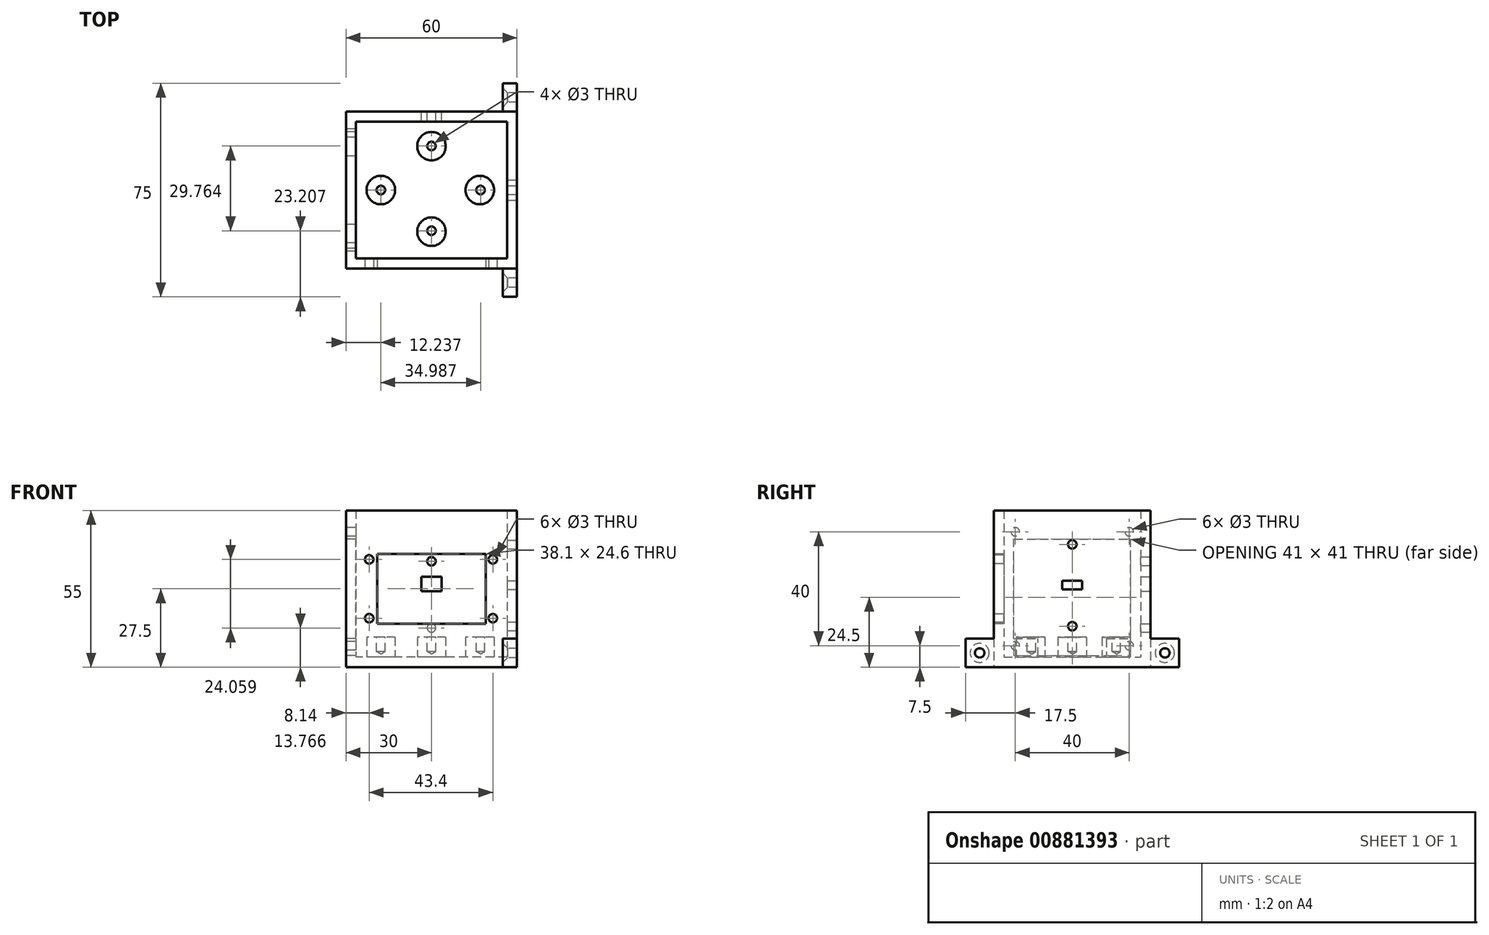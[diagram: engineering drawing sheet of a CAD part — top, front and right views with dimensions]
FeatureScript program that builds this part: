
annotation { "Feature Type Name" : "Feature", "Feature Type Description" : "" }
export const myFeature = defineFeature(function(context is Context, id is Id, definition is map)
    precondition{}
    {
        {
            var Q0;
            Q0=qCreatedBy(makeId("Top.planeOp"),FACE);
            var sketch = newSketch(context, id + "F0", { "sketchPlane" : qUnion([Q0])});
            skLineSegment(sketch, "E0.bottom", {"start": v(30, -27.5) * mm, "end": v(-30, -27.5) * mm});
            skLineSegment(sketch, "E0.top", {"start": v(30, 27.5) * mm, "end": v(-30, 27.5) * mm});
            skLineSegment(sketch, "E0.left", {"start": v(30, -27.5) * mm, "end": v(30, 27.5) * mm});
            skLineSegment(sketch, "E0.right", {"start": v(-30, -27.5) * mm, "end": v(-30, 27.5) * mm});
            skPoint(sketch, "E0.middle", {"position": v(0, 0) * mm});
            skSolve(sketch);
        }
        {
            var Q0;
            Q0=makeQuery(id+"F0.imprint","IMPRINT",FACE,{"disambiguationData":[TD([[makeQuery(id+"F0.imprint","IMPRINT",EDGE,{"derivedFrom":sQuery(id+"F0.wireOp",EDGE,"E0.bottom")}),-1.0]])]});
            extrude(context, id + "F1", {"entities" : qUnion([Q0]), "depth" : 55 * mm, "offsetDistance" : 25 * mm});
        }
        {
            var Q0;
            Q0=makeQuery(id+"F1.opExtrude","CAP_FACE",FACE,{"disambiguationData":[OSD([sQuery(id+"F0.wireOp",EDGE,"E0.bottom"),sQuery(id+"F0.wireOp",EDGE,"E0.top"),sQuery(id+"F0.wireOp",EDGE,"E0.left"),sQuery(id+"F0.wireOp",EDGE,"E0.right")])],"isStart":false});
            shell(context, id + "F2", {"entities" : qUnion([Q0]), "thickness" : 3.5 * mm});
        }
        {
            var Q0;
            Q0=makeQuery(id+"F1.opExtrude","SWEPT_FACE",FACE,{"disambiguationData":[OSD([sQuery(id+"F0.wireOp",EDGE,"E0.bottom")])]});
            var sketch = newSketch(context, id + "F3", { "sketchPlane" : qUnion([Q0])});
            skPoint(sketch, "E1", {"position": v(0, 27.5) * mm});
            skPoint(sketch, "E2", {"position": v(0, 39.8) * mm});
            skPoint(sketch, "E3", {"position": v(0, 15.2) * mm});
            skPoint(sketch, "E4", {"position": v(-19.05, 39.8) * mm});
            skPoint(sketch, "E5", {"position": v(19.05, 39.8) * mm});
            skPoint(sketch, "E6", {"position": v(-19.05, 15.2) * mm});
            skPoint(sketch, "E7", {"position": v(19.05, 15.2) * mm});
            skLineSegment(sketch, "E8", {"start": v(-19.05, 39.8) * mm, "end": v(-19.05, 15.2) * mm});
            skLineSegment(sketch, "E9", {"start": v(0, 15.2) * mm, "end": v(-19.05, 15.2) * mm});
            skLineSegment(sketch, "E10", {"start": v(0, 15.2) * mm, "end": v(19.05, 15.2) * mm});
            skLineSegment(sketch, "E11", {"start": v(19.05, 15.2) * mm, "end": v(19.05, 39.8) * mm});
            skLineSegment(sketch, "E12", {"start": v(-19.05, 39.8) * mm, "end": v(19.05, 39.8) * mm});
            skSolve(sketch);
        }
        {
            var Q0;
            Q0=makeQuery(id+"F3.imprint","IMPRINT",FACE,{"disambiguationData":[TD([[makeQuery(id+"F3.imprint","IMPRINT",EDGE,{"derivedFrom":sQuery(id+"F3.wireOp",EDGE,"E8")}),1.0]])]});
            extrude(context, id + "F4", {"entities" : qUnion([Q0]), "operationType" : NewBodyOperationType.REMOVE, "oppositeDirection" : true, "depth" : 5 * mm, "offsetDistance" : 25 * mm});
        }
        {
            var Q0;
            Q0=makeQuery(id+"F1.opExtrude","SWEPT_FACE",FACE,{"disambiguationData":[OSD([sQuery(id+"F0.wireOp",EDGE,"E0.bottom")])]});
            var sketch = newSketch(context, id + "F5", { "sketchPlane" : qUnion([Q0])});
            skPoint(sketch, "E13", {"position": v(21.54, 37.82) * mm});
            skPoint(sketch, "E14", {"position": v(21.54, 17.17) * mm});
            skPoint(sketch, "E15", {"position": v(-21.86, 17.17) * mm});
            skPoint(sketch, "E16", {"position": v(-21.86, 37.82) * mm});
            skPoint(sketch, "E17", {"position": v(19.05, 27.5) * mm});
            skPoint(sketch, "E18", {"position": v(21.54, 27.5) * mm});
            skSolve(sketch);
        }
        {
            var Q0;
            Q0=sQuery(id+"F5.wireOp",VERTEX,"E16");
            var Q1;
            Q1=sQuery(id+"F5.wireOp",VERTEX,"E15");
            var Q2;
            Q2=sQuery(id+"F5.wireOp",VERTEX,"E14");
            var Q3;
            Q3=sQuery(id+"F5.wireOp",VERTEX,"E13");
            var Q4;
            Q4=makeQuery(id+"F1.opExtrude","SWEPT_BODY",BODY,{"disambiguationData":[OSD([sQuery(id+"F0.wireOp",EDGE,"E0.bottom"),sQuery(id+"F0.wireOp",EDGE,"E0.top"),sQuery(id+"F0.wireOp",EDGE,"E0.left"),sQuery(id+"F0.wireOp",EDGE,"E0.right")])]});
            hole(context, id + "F6", {"style" : HoleStyle.SIMPLE, "endStyle" : HoleEndStyle.BLIND, "holeDiameter" : 3 * mm, "majorDiameter" : 5 * mm, "holeDepth" : 12 * mm, "isTappedThrough" : true, "tappedDepth" : 12 * mm, "tapClearance" : 3, "startFromSketch" : true, "locations" : qUnion([Q0, Q1, Q2, Q3]), "scope" : qUnion([Q4])});
        }
        {
            var Q0;
            Q0=makeQuery(id+"F1.opExtrude","SWEPT_FACE",FACE,{"disambiguationData":[OSD([sQuery(id+"F0.wireOp",EDGE,"E0.right")])]});
            var sketch = newSketch(context, id + "F7", { "sketchPlane" : qUnion([Q0])});
            skPoint(sketch, "E19", {"position": v(0, 27.5) * mm});
            skLineSegment(sketch, "E20.bottom", {"start": v(20.5, 10) * mm, "end": v(-20.5, 10) * mm});
            skLineSegment(sketch, "E20.top", {"start": v(20.5, 45) * mm, "end": v(-20.5, 45) * mm});
            skLineSegment(sketch, "E20.left", {"start": v(20.5, 10) * mm, "end": v(20.5, 45) * mm});
            skLineSegment(sketch, "E20.right", {"start": v(-20.5, 10) * mm, "end": v(-20.5, 45) * mm});
            skPoint(sketch, "E21", {"position": v(20, 27.5) * mm});
            skPoint(sketch, "E22", {"position": v(20, 47.5) * mm});
            skPoint(sketch, "E23", {"position": v(20, 7.5) * mm});
            skPoint(sketch, "E24", {"position": v(-20, 47.5) * mm});
            skPoint(sketch, "E25", {"position": v(-20, 7.5) * mm});
            skPoint(sketch, "E26", {"position": v(0, 7.5) * mm});
            skPoint(sketch, "E27", {"position": v(0, 47.5) * mm});
            skSolve(sketch);
        }
        {
            var Q0;
            Q0=sQuery(id+"F7.wireOp",VERTEX,"E24");
            var Q1;
            Q1=sQuery(id+"F7.wireOp",VERTEX,"E25");
            var Q2;
            Q2=sQuery(id+"F7.wireOp",VERTEX,"E23");
            var Q3;
            Q3=sQuery(id+"F7.wireOp",VERTEX,"E22");
            var Q4;
            Q4=makeQuery(id+"F1.opExtrude","SWEPT_BODY",BODY,{"disambiguationData":[OSD([sQuery(id+"F0.wireOp",EDGE,"E0.bottom"),sQuery(id+"F0.wireOp",EDGE,"E0.top"),sQuery(id+"F0.wireOp",EDGE,"E0.left"),sQuery(id+"F0.wireOp",EDGE,"E0.right")])]});
            hole(context, id + "F8", {"style" : HoleStyle.SIMPLE, "endStyle" : HoleEndStyle.BLIND, "holeDiameter" : 3 * mm, "majorDiameter" : 5 * mm, "holeDepth" : 12 * mm, "isTappedThrough" : true, "tappedDepth" : 12 * mm, "tapClearance" : 3, "startFromSketch" : true, "locations" : qUnion([Q0, Q1, Q2, Q3]), "scope" : qUnion([Q4])});
        }
        {
            var Q0;
            Q0=qSketchRegion(id+"F7",true);
            extrude(context, id + "F9", {"entities" : qUnion([Q0]), "operationType" : NewBodyOperationType.REMOVE, "oppositeDirection" : true, "depth" : 25 * mm, "offsetDistance" : 25 * mm});
        }
        {
            var Q0;
            Q0=makeQuery(id+"F2.opShell","OFFSET_FACE",FACE,{"disambiguationData":[OSD([sQuery(id+"F0.wireOp",EDGE,"E0.bottom"),sQuery(id+"F0.wireOp",EDGE,"E0.top"),sQuery(id+"F0.wireOp",EDGE,"E0.left"),sQuery(id+"F0.wireOp",EDGE,"E0.right")])]});
            var sketch = newSketch(context, id + "F10", { "sketchPlane" : qUnion([Q0])});
            skPoint(sketch, "E28", {"position": v(0, 15.4) * mm});
            skPoint(sketch, "E29", {"position": v(-17.76, 0) * mm});
            skPoint(sketch, "E30", {"position": v(16.97, 0) * mm});
            skPoint(sketch, "E31", {"position": v(0, -14.6) * mm});
            skCircle(sketch, "E32", {"center": v(0, 15.4) * mm, "radius": 5 * mm});
            skCircle(sketch, "E33", {"center": v(-17.76, 0) * mm, "radius": 5 * mm});
            skCircle(sketch, "E34", {"center": v(0, -14.6) * mm, "radius": 5 * mm});
            skCircle(sketch, "E35", {"center": v(16.97, 0) * mm, "radius": 5 * mm});
            skSolve(sketch);
        }
        {
            var Q0;
            Q0=makeQuery(id+"F10.imprint","IMPRINT",FACE,{"disambiguationData":[TD([[makeQuery(id+"F10.imprint","IMPRINT",EDGE,{"derivedFrom":sQuery(id+"F10.wireOp",EDGE,"E33")}),1.0]])]});
            var Q1;
            Q1=makeQuery(id+"F10.imprint","IMPRINT",FACE,{"disambiguationData":[TD([[makeQuery(id+"F10.imprint","IMPRINT",EDGE,{"derivedFrom":sQuery(id+"F10.wireOp",EDGE,"E32")}),1.0]])]});
            var Q2;
            Q2=makeQuery(id+"F10.imprint","IMPRINT",FACE,{"disambiguationData":[TD([[makeQuery(id+"F10.imprint","IMPRINT",EDGE,{"derivedFrom":sQuery(id+"F10.wireOp",EDGE,"E35")}),1.0]])]});
            var Q3;
            Q3=makeQuery(id+"F10.imprint","IMPRINT",FACE,{"disambiguationData":[TD([[makeQuery(id+"F10.imprint","IMPRINT",EDGE,{"derivedFrom":sQuery(id+"F10.wireOp",EDGE,"E34")}),1.0]])]});
            extrude(context, id + "F11", {"entities" : qUnion([Q0, Q1, Q2, Q3]), "operationType" : NewBodyOperationType.ADD, "depth" : 7 * mm, "offsetDistance" : 25 * mm});
        }
        {
            var Q0;
            Q0=makeQuery(id+"F11.opExtrude","CAP_FACE",FACE,{"disambiguationData":[OSD([sQuery(id+"F10.wireOp",EDGE,"E33")])],"isStart":false});
            var sketch = newSketch(context, id + "F12", { "sketchPlane" : qUnion([Q0])});
            skPoint(sketch, "E36", {"position": v(-17.76, 0) * mm});
            skPoint(sketch, "E37", {"position": v(0, 15.47) * mm});
            skPoint(sketch, "E38", {"position": v(17.22, 0) * mm});
            skPoint(sketch, "E39", {"position": v(0, -14.3) * mm});
            skSolve(sketch);
        }
        {
            var Q0;
            Q0=sQuery(id+"F12.wireOp",VERTEX,"E37");
            var Q1;
            Q1=sQuery(id+"F12.wireOp",VERTEX,"E36");
            var Q2;
            Q2=sQuery(id+"F12.wireOp",VERTEX,"E39");
            var Q3;
            Q3=sQuery(id+"F12.wireOp",VERTEX,"E38");
            var Q4;
            Q4=makeQuery(id+"F1.opExtrude","SWEPT_BODY",BODY,{"disambiguationData":[OSD([sQuery(id+"F0.wireOp",EDGE,"E0.bottom"),sQuery(id+"F0.wireOp",EDGE,"E0.top"),sQuery(id+"F0.wireOp",EDGE,"E0.left"),sQuery(id+"F0.wireOp",EDGE,"E0.right")])]});
            hole(context, id + "F13", {"style" : HoleStyle.SIMPLE, "endStyle" : HoleEndStyle.BLIND, "holeDiameter" : 3 * mm, "majorDiameter" : 5 * mm, "holeDepth" : 5 * mm, "isTappedThrough" : true, "tappedDepth" : 12 * mm, "tapClearance" : 3, "startFromSketch" : true, "locations" : qUnion([Q0, Q1, Q2, Q3]), "scope" : qUnion([Q4])});
        }
        {
            var Q0;
            Q0=makeQuery(id+"F1.opExtrude","SWEPT_FACE",FACE,{"disambiguationData":[OSD([sQuery(id+"F0.wireOp",EDGE,"E0.left")])]});
            var sketch = newSketch(context, id + "F14", { "sketchPlane" : qUnion([Q0])});
            skLineSegment(sketch, "E40.bottom", {"start": v(3.5, 27.31) * mm, "end": v(-3.5, 27.31) * mm});
            skLineSegment(sketch, "E40.top", {"start": v(3.5, 30.31) * mm, "end": v(-3.5, 30.31) * mm});
            skLineSegment(sketch, "E40.left", {"start": v(3.5, 27.31) * mm, "end": v(3.5, 30.31) * mm});
            skLineSegment(sketch, "E40.right", {"start": v(-3.5, 27.31) * mm, "end": v(-3.5, 30.31) * mm});
            skPoint(sketch, "E40.middle", {"position": v(0, 28.81) * mm});
            skPoint(sketch, "E41", {"position": v(0, 48.81) * mm});
            skPoint(sketch, "E42", {"position": v(15, 48.81) * mm});
            skPoint(sketch, "E43", {"position": v(-15, 48.81) * mm});
            skPoint(sketch, "E44", {"position": v(0, 8.81) * mm});
            skPoint(sketch, "E45", {"position": v(-15, 8.81) * mm});
            skPoint(sketch, "E46", {"position": v(15, 8.81) * mm});
            skCircle(sketch, "E47", {"center": v(-15, 48.81) * mm, "radius": 2 * mm});
            skCircle(sketch, "E48", {"center": v(15, 48.81) * mm, "radius": 2 * mm});
            skCircle(sketch, "E49", {"center": v(0, 48.81) * mm, "radius": 2 * mm});
            skCircle(sketch, "E50", {"center": v(-15, 8.81) * mm, "radius": 2 * mm});
            skCircle(sketch, "E51", {"center": v(0, 8.81) * mm, "radius": 2 * mm});
            skCircle(sketch, "E52", {"center": v(15, 8.81) * mm, "radius": 2 * mm});
            skSolve(sketch);
        }
        {
            var Q0;
            Q0=makeQuery(id+"F14.imprint","IMPRINT",FACE,{"disambiguationData":[TD([[makeQuery(id+"F14.imprint","IMPRINT",EDGE,{"derivedFrom":sQuery(id+"F14.wireOp",EDGE,"E40.bottom")}),-1.0]])]});
            extrude(context, id + "F15", {"entities" : qUnion([Q0]), "operationType" : NewBodyOperationType.REMOVE, "oppositeDirection" : true, "depth" : 5 * mm, "offsetDistance" : 25 * mm});
        }
        {
            var Q0;
            Q0=makeQuery(id+"F1.opExtrude","SWEPT_FACE",FACE,{"disambiguationData":[OSD([sQuery(id+"F0.wireOp",EDGE,"E0.top")])]});
            var sketch = newSketch(context, id + "F16", { "sketchPlane" : qUnion([Q0])});
            skLineSegment(sketch, "E53.bottom", {"start": v(3.5, 26.7) * mm, "end": v(-3.5, 26.7) * mm});
            skLineSegment(sketch, "E53.top", {"start": v(3.5, 31.7) * mm, "end": v(-3.5, 31.7) * mm});
            skLineSegment(sketch, "E53.left", {"start": v(3.5, 26.7) * mm, "end": v(3.5, 31.7) * mm});
            skLineSegment(sketch, "E53.right", {"start": v(-3.5, 26.7) * mm, "end": v(-3.5, 31.7) * mm});
            skPoint(sketch, "E53.middle", {"position": v(0, 29.2) * mm});
            skSolve(sketch);
        }
        {
            var Q0;
            Q0=makeQuery(id+"F16.imprint","IMPRINT",FACE,{"disambiguationData":[TD([[makeQuery(id+"F16.imprint","IMPRINT",EDGE,{"derivedFrom":sQuery(id+"F16.wireOp",EDGE,"E53.bottom")}),-1.0]])]});
            extrude(context, id + "F17", {"entities" : qUnion([Q0]), "operationType" : NewBodyOperationType.REMOVE, "oppositeDirection" : true, "depth" : 5 * mm, "offsetDistance" : 25 * mm});
        }
        {
            var Q0;
            Q0=makeQuery(id+"F1.opExtrude","SWEPT_FACE",FACE,{"disambiguationData":[OSD([sQuery(id+"F0.wireOp",EDGE,"E0.right")])]});
            var sketch = newSketch(context, id + "F18", { "sketchPlane" : qUnion([Q0])});
            skPoint(sketch, "E54", {"position": v(0, 10) * mm});
            skPoint(sketch, "E55", {"position": v(12, 10) * mm});
            skPoint(sketch, "E56", {"position": v(-12, 10) * mm});
            skPoint(sketch, "E57", {"position": v(-12, 4) * mm});
            skPoint(sketch, "E58", {"position": v(12, 4) * mm});
            skLineSegment(sketch, "E59", {"start": v(-12, 10) * mm, "end": v(-12, 4) * mm});
            skLineSegment(sketch, "E60", {"start": v(12, 4) * mm, "end": v(-12, 4) * mm});
            skLineSegment(sketch, "E61", {"start": v(12, 4) * mm, "end": v(12, 10) * mm});
            skSolve(sketch);
        }
        {
            var Q0;
            {var subQ0=sQuery(id+"F18.wireOp",EDGE,"E59");Q0=makeQuery(id+"F18.imprint","IMPRINT",FACE,{"disambiguationData":[TD([[makeQuery(id+"F18.imprint","IMPRINT",EDGE,{"derivedFrom":subQ0}),1.0]])]});}
            extrude(context, id + "F19", {"entities" : qUnion([Q0]), "operationType" : NewBodyOperationType.REMOVE, "oppositeDirection" : true, "depth" : 4 * mm, "offsetDistance" : 25 * mm});
        }
        {
            var Q0;
            Q0=makeQuery(id+"F1.opExtrude","SWEPT_FACE",FACE,{"disambiguationData":[OSD([sQuery(id+"F0.wireOp",EDGE,"E0.left")])]});
            var sketch = newSketch(context, id + "F20", { "sketchPlane" : qUnion([Q0])});
            skPoint(sketch, "E62", {"position": v(0, 43.08) * mm});
            skPoint(sketch, "E63", {"position": v(0, 14.36) * mm});
            skSolve(sketch);
        }
        {
            var Q0;
            Q0=sQuery(id+"F20.wireOp",VERTEX,"E62");
            var Q1;
            Q1=sQuery(id+"F20.wireOp",VERTEX,"E63");
            var Q2;
            Q2=makeQuery(id+"F1.opExtrude","SWEPT_BODY",BODY,{"disambiguationData":[OSD([sQuery(id+"F0.wireOp",EDGE,"E0.bottom"),sQuery(id+"F0.wireOp",EDGE,"E0.top"),sQuery(id+"F0.wireOp",EDGE,"E0.left"),sQuery(id+"F0.wireOp",EDGE,"E0.right")])]});
            hole(context, id + "F21", {"style" : HoleStyle.SIMPLE, "endStyle" : HoleEndStyle.BLIND, "holeDiameter" : 3 * mm, "majorDiameter" : 5 * mm, "holeDepth" : 5 * mm, "isTappedThrough" : true, "tappedDepth" : 12 * mm, "tapClearance" : 3, "startFromSketch" : true, "locations" : qUnion([Q0, Q1]), "scope" : qUnion([Q2])});
        }
        {
            var Q0;
            Q0=makeQuery(id+"F1.opExtrude","SWEPT_FACE",FACE,{"disambiguationData":[OSD([sQuery(id+"F0.wireOp",EDGE,"E0.top")])]});
            var sketch = newSketch(context, id + "F22", { "sketchPlane" : qUnion([Q0])});
            skPoint(sketch, "E64", {"position": v(0, 37.18) * mm});
            skPoint(sketch, "E65", {"position": v(0, 13.77) * mm});
            skPoint(sketch, "E66", {"position": v(20, 3) * mm});
            skPoint(sketch, "E67", {"position": v(-20, 3) * mm});
            skLineSegment(sketch, "E68", {"start": v(-20, 3) * mm, "end": v(-30, 3) * mm});
            skLineSegment(sketch, "E69", {"start": v(-30, 3) * mm, "end": v(-20, 3) * mm});
            skLineSegment(sketch, "E70", {"start": v(-20, 0) * mm, "end": v(-20, 3) * mm});
            skLineSegment(sketch, "E71", {"start": v(20, 3) * mm, "end": v(20, 0) * mm});
            skLineSegment(sketch, "E72", {"start": v(20, 3) * mm, "end": v(30, 3) * mm});
            skSolve(sketch);
        }
        {
            var Q0;
            Q0=sQuery(id+"F22.wireOp",VERTEX,"E64");
            var Q1;
            Q1=sQuery(id+"F22.wireOp",VERTEX,"E65");
            var Q2;
            Q2=makeQuery(id+"F1.opExtrude","SWEPT_BODY",BODY,{"disambiguationData":[OSD([sQuery(id+"F0.wireOp",EDGE,"E0.bottom"),sQuery(id+"F0.wireOp",EDGE,"E0.top"),sQuery(id+"F0.wireOp",EDGE,"E0.left"),sQuery(id+"F0.wireOp",EDGE,"E0.right")])]});
            hole(context, id + "F23", {"style" : HoleStyle.SIMPLE, "endStyle" : HoleEndStyle.BLIND, "holeDiameter" : 3 * mm, "majorDiameter" : 5 * mm, "holeDepth" : 5 * mm, "isTappedThrough" : true, "tappedDepth" : 12 * mm, "tapClearance" : 3, "startFromSketch" : true, "locations" : qUnion([Q0, Q1]), "scope" : qUnion([Q2])});
        }
        {
            var Q0;
            Q0=makeQuery(id+"F3.imprint","IMPRINT",FACE,{"disambiguationData":[TD([[makeQuery(id+"F3.imprint","IMPRINT",EDGE,{"derivedFrom":sQuery(id+"F3.wireOp",EDGE,"E8")}),-1.0]])]});
            var sketch = newSketch(context, id + "F24", { "sketchPlane" : qUnion([Q0])});
            skPoint(sketch, "E73", {"position": v(25, 10) * mm});
            skLineSegment(sketch, "E74", {"start": v(25, 10) * mm, "end": v(25, 0) * mm});
            skLineSegment(sketch, "E75", {"start": v(25, 10) * mm, "end": v(30, 10) * mm});
            skSolve(sketch);
        }
        {
            var Q0;
            {var subQ0=sQuery(id+"F24.wireOp",EDGE,"E74");Q0=makeQuery(id+"F24.imprint","IMPRINT",FACE,{"disambiguationData":[TD([[makeQuery(id+"F24.imprint","IMPRINT",EDGE,{"derivedFrom":subQ0}),1.0]])]});}
            extrude(context, id + "F25", {"entities" : qUnion([Q0]), "operationType" : NewBodyOperationType.ADD, "depth" : 10 * mm, "offsetDistance" : 25 * mm});
        }
        {
            var Q0;
            Q0=makeQuery(id+"F25.opExtrude","SWEPT_FACE",FACE,{"disambiguationData":[OSD([sQuery(id+"F24.wireOp",EDGE,"E74")])]});
            var sketch = newSketch(context, id + "F26", { "sketchPlane" : qUnion([Q0])});
            skPoint(sketch, "E76", {"position": v(32.5, 5) * mm});
            skPoint(sketch, "E76.positionSnap0", {"position": v(32.5, 10) * mm});
            skPoint(sketch, "E76.positionSnap1", {"position": v(27.5, 5) * mm});
            skSolve(sketch);
        }
        {
            var Q0;
            Q0=sQuery(id+"F26.wireOp",VERTEX,"E76");
            var Q1;
            Q1=makeQuery(id+"F1.opExtrude","SWEPT_BODY",BODY,{"disambiguationData":[OSD([sQuery(id+"F0.wireOp",EDGE,"E0.bottom"),sQuery(id+"F0.wireOp",EDGE,"E0.top"),sQuery(id+"F0.wireOp",EDGE,"E0.left"),sQuery(id+"F0.wireOp",EDGE,"E0.right")])]});
            hole(context, id + "F27", {"style" : HoleStyle.C_SINK, "endStyle" : HoleEndStyle.BLIND, "standardTappedOrClearance" : lookupTablePath({ "standard" : "ISO", "fit" : "Normal", "size" : "M3", "type" : "Clearance" }), "standardBlindInLast" : lookupTablePath({ "fit" : "Standard", "standard" : "ISO", "size" : "M3", "type" : "Clearance" }), "holeDiameter" : 3.3 * mm, "cSinkDiameter" : 6.72 * mm, "cSinkAngle" : 90 * degree, "majorDiameter" : 5 * mm, "holeDepth" : 5 * mm, "isTappedThrough" : true, "tappedDepth" : 12 * mm, "tapClearance" : 3, "startFromSketch" : true, "locations" : qUnion([Q0]), "scope" : qUnion([Q1])});
        }
        {
            var Q0;
            Q0=makeQuery(id+"F1.opExtrude","SWEPT_FACE",FACE,{"disambiguationData":[OSD([sQuery(id+"F0.wireOp",EDGE,"E0.top")])]});
            var sketch = newSketch(context, id + "F28", { "sketchPlane" : qUnion([Q0])});
            skPoint(sketch, "E77", {"position": v(-25, 10) * mm});
            skLineSegment(sketch, "E78.bottom", {"start": v(-25, 10) * mm, "end": v(-30, 10) * mm});
            skLineSegment(sketch, "E78.top", {"start": v(-25, 0) * mm, "end": v(-30, 0) * mm});
            skLineSegment(sketch, "E78.left", {"start": v(-25, 10) * mm, "end": v(-25, 0) * mm});
            skLineSegment(sketch, "E78.right", {"start": v(-30, 10) * mm, "end": v(-30, 0) * mm});
            skSolve(sketch);
        }
        {
            var Q0;
            Q0=makeQuery(id+"F28.imprint","IMPRINT",FACE,{"disambiguationData":[TD([[makeQuery(id+"F28.imprint","IMPRINT",EDGE,{"derivedFrom":sQuery(id+"F28.wireOp",EDGE,"E78.bottom")}),1.0]])]});
            extrude(context, id + "F29", {"entities" : qUnion([Q0]), "operationType" : NewBodyOperationType.ADD, "depth" : 10 * mm, "offsetDistance" : 25 * mm});
        }
        {
            var Q0;
            Q0=makeQuery(id+"F29.opExtrude","SWEPT_FACE",FACE,{"disambiguationData":[OSD([sQuery(id+"F28.wireOp",EDGE,"E78.left")])]});
            var sketch = newSketch(context, id + "F30", { "sketchPlane" : qUnion([Q0])});
            skPoint(sketch, "E79", {"position": v(-32.5, 5) * mm});
            skPoint(sketch, "E79.positionSnap0", {"position": v(-32.5, 10) * mm});
            skPoint(sketch, "E79.positionSnap1", {"position": v(-37.5, 5) * mm});
            skSolve(sketch);
        }
        {
            var Q0;
            Q0=sQuery(id+"F30.wireOp",VERTEX,"E79");
            var Q1;
            Q1=makeQuery(id+"F1.opExtrude","SWEPT_BODY",BODY,{"disambiguationData":[OSD([sQuery(id+"F0.wireOp",EDGE,"E0.bottom"),sQuery(id+"F0.wireOp",EDGE,"E0.top"),sQuery(id+"F0.wireOp",EDGE,"E0.left"),sQuery(id+"F0.wireOp",EDGE,"E0.right")])]});
            hole(context, id + "F31", {"style" : HoleStyle.C_SINK, "endStyle" : HoleEndStyle.BLIND, "standardTappedOrClearance" : lookupTablePath({ "standard" : "ISO", "fit" : "Normal", "size" : "M3", "type" : "Clearance" }), "standardBlindInLast" : lookupTablePath({ "fit" : "Standard", "standard" : "ISO", "size" : "M3", "type" : "Clearance" }), "holeDiameter" : 3.3 * mm, "cSinkDiameter" : 6.72 * mm, "cSinkAngle" : 90 * degree, "majorDiameter" : 5 * mm, "holeDepth" : 5 * mm, "isTappedThrough" : true, "tappedDepth" : 12 * mm, "tapClearance" : 3, "startFromSketch" : true, "locations" : qUnion([Q0]), "scope" : qUnion([Q1])});
        }
    });
